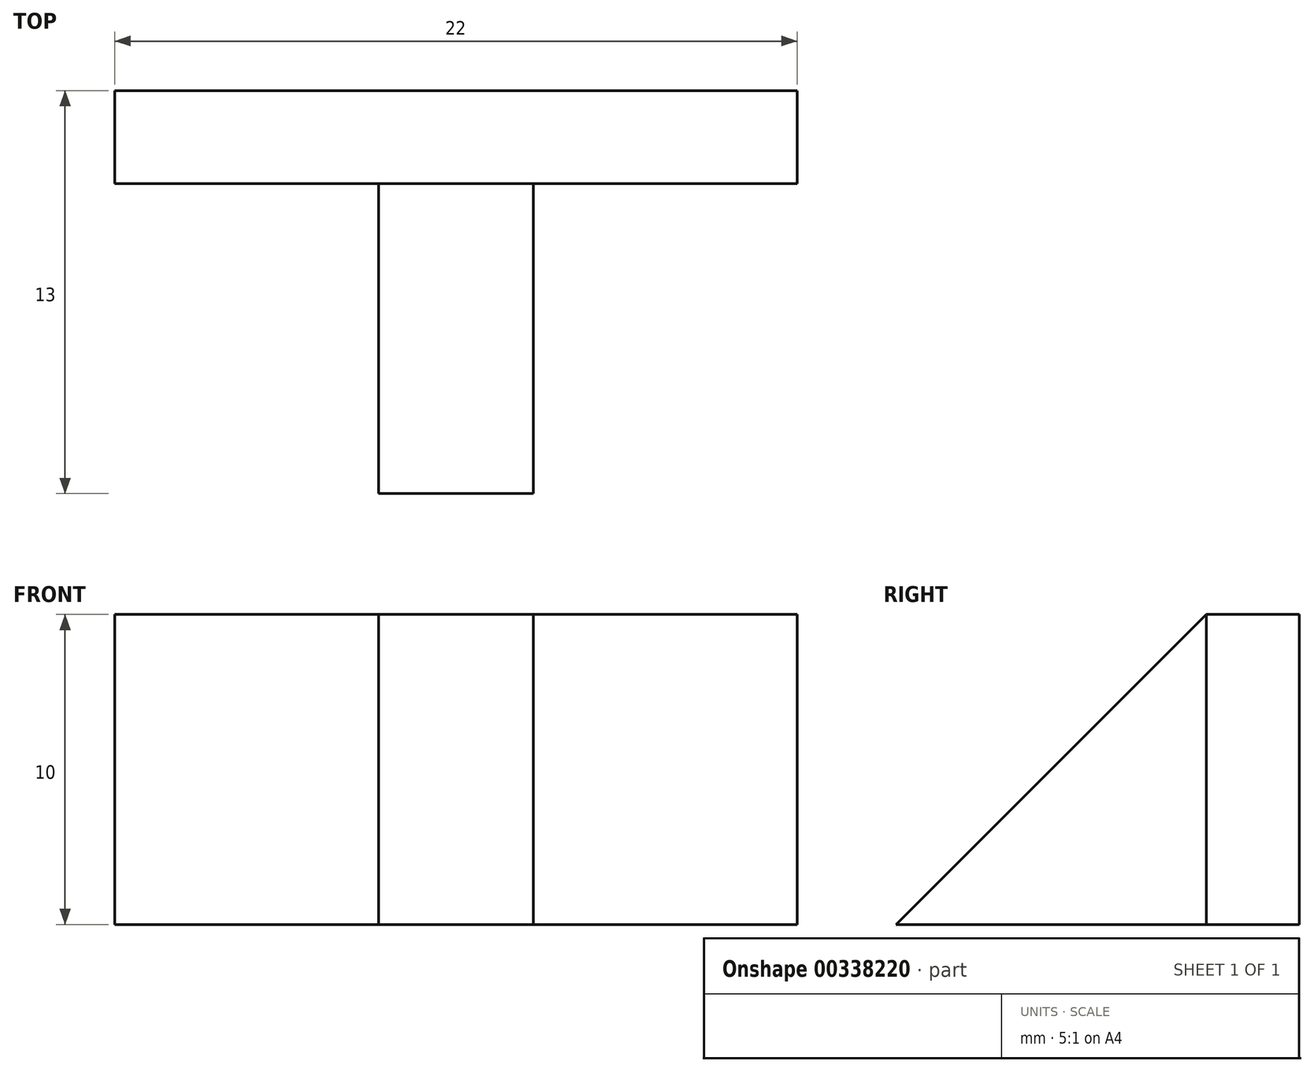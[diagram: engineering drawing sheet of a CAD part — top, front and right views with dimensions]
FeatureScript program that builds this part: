
annotation { "Feature Type Name" : "Feature", "Feature Type Description" : "" }
export const myFeature = defineFeature(function(context is Context, id is Id, definition is map)
    precondition{}
    {
        {
            var Q0;
            Q0=qCreatedBy(makeId("Top.planeOp"),FACE);
            var sketch = newSketch(context, id + "F0", { "sketchPlane" : qUnion([Q0])});
            skLineSegment(sketch, "E0.bottom", {"start": v(0, 0) * mm, "end": v(22, 0) * mm});
            skLineSegment(sketch, "E0.top", {"start": v(0, -3) * mm, "end": v(22, -3) * mm});
            skLineSegment(sketch, "E0.left", {"start": v(0, 0) * mm, "end": v(0, -3) * mm});
            skLineSegment(sketch, "E0.right", {"start": v(22, 0) * mm, "end": v(22, -3) * mm});
            skLineSegment(sketch, "E1.bottom", {"start": v(8.5, -3) * mm, "end": v(13.5, -3) * mm});
            skLineSegment(sketch, "E1.top", {"start": v(8.5, -13) * mm, "end": v(13.5, -13) * mm});
            skLineSegment(sketch, "E1.left", {"start": v(8.5, -3) * mm, "end": v(8.5, -13) * mm});
            skLineSegment(sketch, "E1.right", {"start": v(13.5, -3) * mm, "end": v(13.5, -13) * mm});
            skPoint(sketch, "E1.middle", {"position": v(11, -8) * mm});
            skPoint(sketch, "E1.middle.positionSnap0", {"position": v(11, -3) * mm});
            skPoint(sketch, "E1.centerSnap0", {"position": v(11, -3) * mm});
            skSolve(sketch);
        }
        {
            var Q0;
            Q0 = qSketchRegion(id + "F0", true);
            extrude(context, id + "F1", {"entities" : qUnion([Q0]), "depth" : 10 * mm});
        }
        {
            var Q0;
            Q0=makeQuery(id+"F1.opExtrude","SWEPT_FACE",FACE,{"disambiguationData":[OSD([sQuery(id+"F0.wireOp",EDGE,"E1.right")])]});
            var sketch = newSketch(context, id + "F2", { "sketchPlane" : qUnion([Q0])});
            skLineSegment(sketch, "E2", {"start": v(-13, 0) * mm, "end": v(-3, 10) * mm});
            skLineSegment(sketch, "E3", {"start": v(-3, 10) * mm, "end": v(-13, 10) * mm});
            skLineSegment(sketch, "E4", {"start": v(-13, 10) * mm, "end": v(-13, 0) * mm});
            skSolve(sketch);
        }
        {
            var Q0;
            Q0 = qSketchRegion(id + "F2", true);
            extrude(context, id + "F3", {"entities" : qUnion([Q0]), "operationType" : NewBodyOperationType.REMOVE, "endBound" : BoundingType.THROUGH_ALL, "oppositeDirection" : true, "depth" : 25 * mm});
        }
    });
